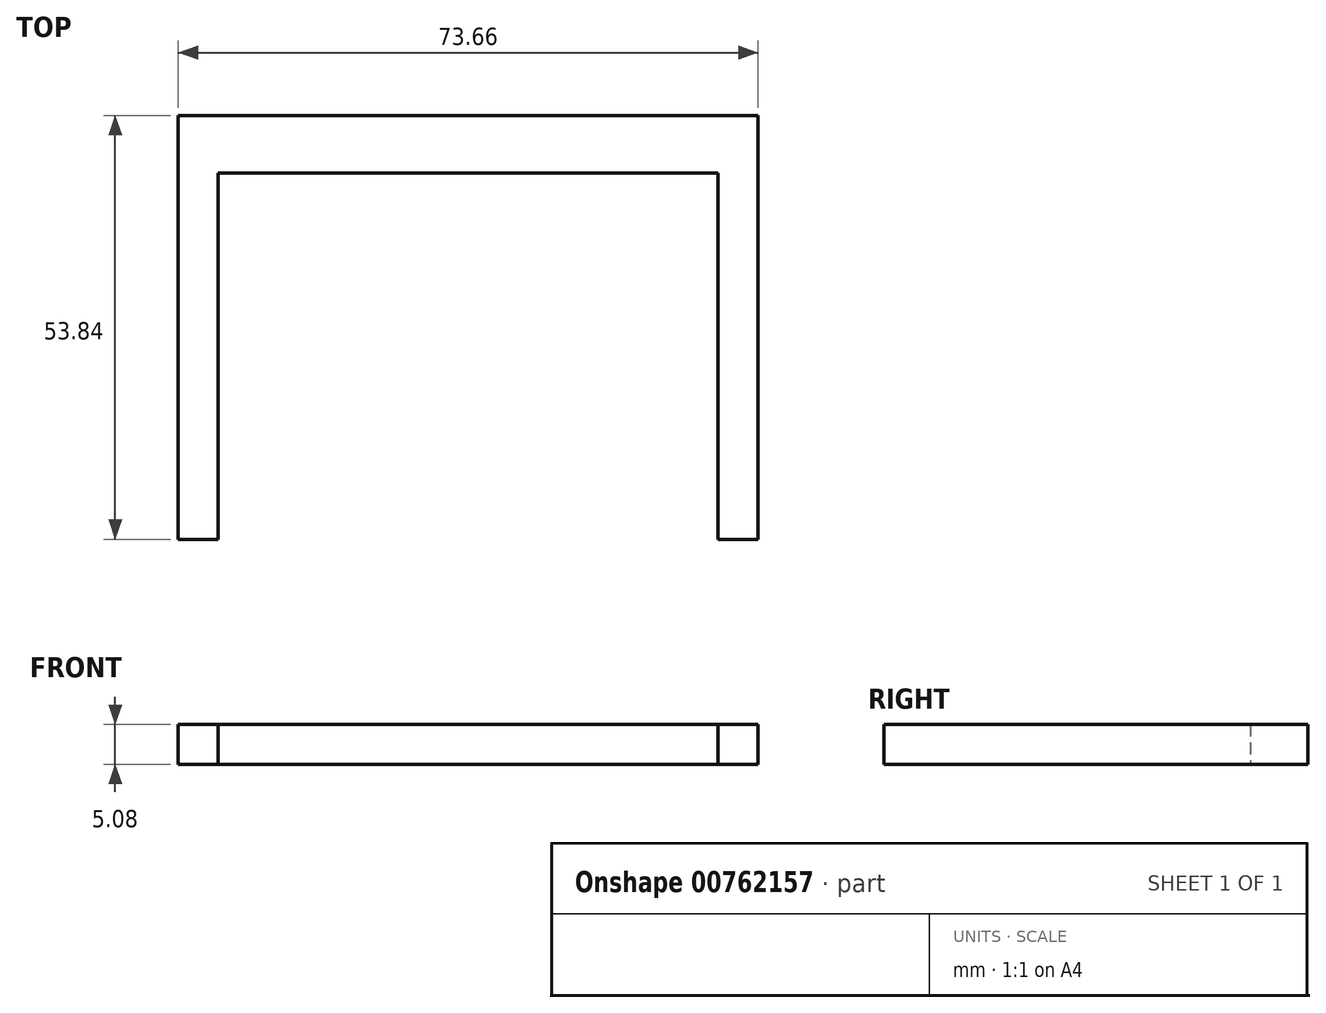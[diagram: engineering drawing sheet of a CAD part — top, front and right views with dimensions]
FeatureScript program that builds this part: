
annotation { "Feature Type Name" : "Feature", "Feature Type Description" : "" }
export const myFeature = defineFeature(function(context is Context, id is Id, definition is map)
    precondition{}
    {
        {
            var Q0;
            Q0=qCreatedBy(makeId("Top.planeOp"),FACE);
            var sketch = newSketch(context, id + "F0", { "sketchPlane" : qUnion([Q0])});
            skLineSegment(sketch, "E0", {"start": v(-18.75, -23.7) * mm, "end": v(-13.67, -23.7) * mm});
            skLineSegment(sketch, "E1", {"start": v(49.83, -23.7) * mm, "end": v(54.91, -23.7) * mm});
            skLineSegment(sketch, "E2", {"start": v(-18.75, -23.7) * mm, "end": v(-18.75, 30.14) * mm});
            skLineSegment(sketch, "E3", {"start": v(-18.75, 30.14) * mm, "end": v(54.91, 30.14) * mm});
            skLineSegment(sketch, "E4", {"start": v(54.91, 30.14) * mm, "end": v(54.91, -23.7) * mm});
            skLineSegment(sketch, "E5", {"start": v(49.83, -23.7) * mm, "end": v(49.83, 22.84) * mm});
            skLineSegment(sketch, "E6", {"start": v(49.83, 22.84) * mm, "end": v(-13.67, 22.84) * mm});
            skLineSegment(sketch, "E7", {"start": v(-13.67, 22.84) * mm, "end": v(-13.67, -23.7) * mm});
            skSolve(sketch);
        }
        {
            var Q0;
            Q0 = qSketchRegion(id + "F0", true);
            extrude(context, id + "F1", {"entities" : qUnion([Q0]), "depth" : 5.08 * mm, "offsetDistance" : 25.4 * mm});
        }
    });
